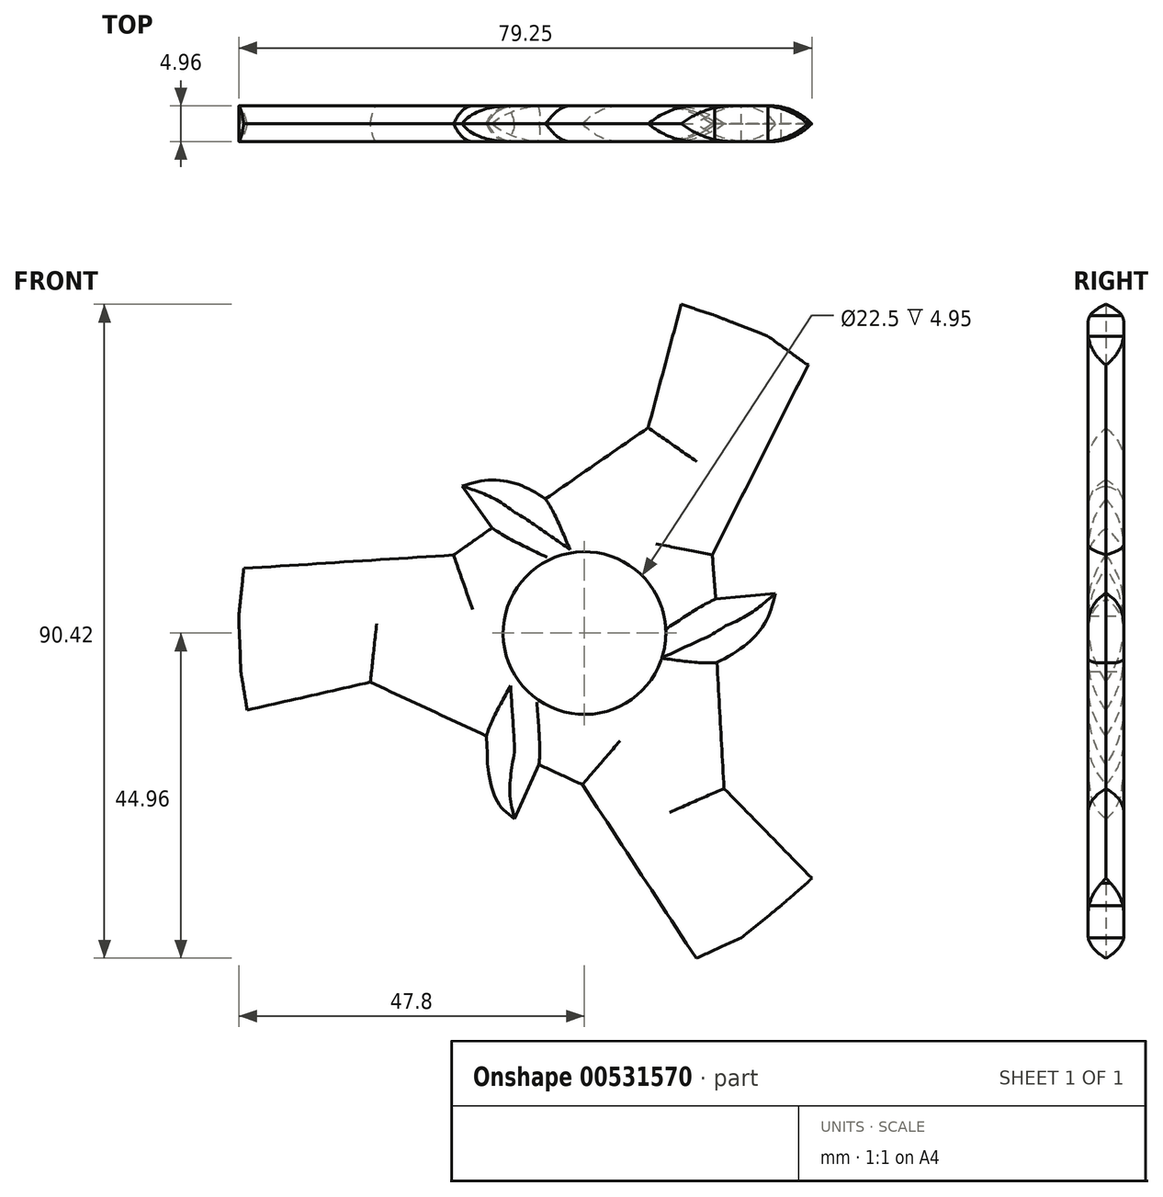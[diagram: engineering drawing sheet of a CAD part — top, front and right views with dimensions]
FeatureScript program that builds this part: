
annotation { "Feature Type Name" : "Feature", "Feature Type Description" : "" }
export const myFeature = defineFeature(function(context is Context, id is Id, definition is map)
    precondition{}
    {
        {
            var Q0;
            Q0=qCreatedBy(makeId("Front.planeOp"),FACE);
            var sketch = newSketch(context, id + "F0", { "sketchPlane" : qUnion([Q0])});
            skLineSegment(sketch, "E0", {"start": v(-60.3, 10.65) * mm, "end": v(-21.94, 13.1) * mm});
            skLineSegment(sketch, "E1", {"start": v(-60.3, 10.65) * mm, "end": v(-61.14, 2.7) * mm});
            skLineSegment(sketch, "E2", {"start": v(-61.14, 2.7) * mm, "end": v(-60.8, -6.3) * mm});
            skLineSegment(sketch, "E3", {"start": v(32.42, 52.48) * mm, "end": v(38.9, 47.8) * mm});
            skLineSegment(sketch, "E4", {"start": v(20.48, -57.17) * mm, "end": v(27.79, -53.9) * mm});
            skLineSegment(sketch, "E5", {"start": v(27.79, -53.9) * mm, "end": v(34.8, -48.28) * mm});
            skLineSegment(sketch, "E6", {"start": v(20.48, -57.17) * mm, "end": v(-0.35, -25.4) * mm});
            skLineSegment(sketch, "E7", {"start": v(-0.35, -25.4) * mm, "end": v(-7.62, -22.05) * mm});
            skLineSegment(sketch, "E8", {"start": v(-35.88, -8.21) * mm, "end": v(-59.64, -13.61) * mm});
            skLineSegment(sketch, "E9", {"start": v(23.4, -26.03) * mm, "end": v(40.2, -43.2) * mm});
            skLineSegment(sketch, "E10", {"start": v(-21.94, 13.1) * mm, "end": v(-15.4, 17.7) * mm});
            skLineSegment(sketch, "E11", {"start": v(10.69, 34.45) * mm, "end": v(17.05, 58.2) * mm});
            skLineSegment(sketch, "E12", {"start": v(17.05, 58.2) * mm, "end": v(32.42, 52.48) * mm});
            skLineSegment(sketch, "E13", {"start": v(40.2, -43.2) * mm, "end": v(34.8, -48.28) * mm});
            skLineSegment(sketch, "E14", {"start": v(-60.8, -6.3) * mm, "end": v(-59.64, -13.61) * mm});
            skPoint(sketch, "E15", {"position": v(-15.4, 17.7) * mm});
            skPoint(sketch, "E16", {"position": v(-7.62, -22.05) * mm});
            skPoint(sketch, "E17", {"position": v(-16.7, -17.87) * mm});
            skLineSegment(sketch, "E18", {"start": v(-57.1, 10.85) * mm, "end": v(-57.94, 2.9) * mm});
            skLineSegment(sketch, "E19", {"start": v(-57.94, 2.9) * mm, "end": v(-57.6, -6.44) * mm});
            skLineSegment(sketch, "E20", {"start": v(-57.6, -6.44) * mm, "end": v(-56.52, -12.9) * mm});
            skLineSegment(sketch, "E21", {"start": v(18.73, -54.5) * mm, "end": v(26.3, -51.08) * mm});
            skLineSegment(sketch, "E22", {"start": v(26.3, -51.08) * mm, "end": v(32.97, -45.66) * mm});
            skLineSegment(sketch, "E23", {"start": v(32.97, -45.66) * mm, "end": v(37.26, -41.92) * mm});
            skLineSegment(sketch, "E24", {"start": v(37.2, 45.1) * mm, "end": v(30.73, 49.77) * mm});
            skLineSegment(sketch, "E25", {"start": v(30.73, 49.77) * mm, "end": v(21.84, 53.25) * mm});
            skLineSegment(sketch, "E26", {"start": v(21.84, 53.25) * mm, "end": v(16.22, 55.1) * mm});
            skLineSegment(sketch, "E27.trimOffspring", {"start": v(21.84, 53.25) * mm, "end": v(22.04, 53.58) * mm});
            skLineSegment(sketch, "E28.trimOffspring", {"start": v(21.43, 13.1) * mm, "end": v(38.9, 47.8) * mm});
            skPoint(sketch, "E29", {"position": v(5.47, -9.54) * mm});
            skPoint(sketch, "E30.end.orphan", {"position": v(23.99, 55.62) * mm});
            skPoint(sketch, "E31", {"position": v(5.53, 9.51) * mm});
            skPoint(sketch, "E32", {"position": v(-11, 0.03) * mm});
            skLineSegment(sketch, "E33", {"start": v(-7.62, -22.05) * mm, "end": v(-11.72, -31.18) * mm});
            skPoint(sketch, "E34", {"position": v(-14, -29.12) * mm});
            skPoint(sketch, "E35", {"position": v(-15.5, -26.06) * mm});
            skPoint(sketch, "E36", {"position": v(-16.25, -22.11) * mm});
            skFitSpline(sketch, "E37", {"points": [v(-11.72, -31.18) * mm, v(-14, -29.12) * mm, v(-15.5, -26.06) * mm, v(-16.25, -22.11) * mm, v(-16.43, -17.26) * mm], "startDerivative": vector(-11.16, 10.33) * mm, "endDerivative": vector(-2.85, 43.72) * mm});
            skLineSegment(sketch, "E38", {"start": v(-16.43, -17.26) * mm, "end": v(-35.88, -8.21) * mm});
            skLineSegment(sketch, "E39", {"start": v(21.99, 5.7) * mm, "end": v(31.95, 6.64) * mm});
            skPoint(sketch, "E40", {"position": v(30.89, 3) * mm});
            skPoint(sketch, "E41", {"position": v(29.02, -0.03) * mm});
            skPoint(sketch, "E42", {"position": v(26.37, -2.45) * mm});
            skFitSpline(sketch, "E43", {"points": [v(31.95, 6.64) * mm, v(30.89, 3) * mm, v(29.02, -0.03) * mm, v(26.37, -2.45) * mm, v(22.2, -4.93) * mm], "startDerivative": vector(-3.5, -14.8) * mm, "endDerivative": vector(-14.01, -6.46) * mm});
            skLineSegment(sketch, "E44", {"start": v(23.4, -26.03) * mm, "end": v(22.2, -4.93) * mm});
            skLineSegment(sketch, "E45", {"start": v(-14.66, 16.51) * mm, "end": v(-20.5, 24.64) * mm});
            skPoint(sketch, "E46", {"position": v(-16.82, 25.56) * mm});
            skPoint(sketch, "E47", {"position": v(-13.27, 25.48) * mm});
            skPoint(sketch, "E48", {"position": v(-9.84, 24.42) * mm});
            skFitSpline(sketch, "E49", {"points": [v(-20.5, 24.64) * mm, v(-16.82, 25.56) * mm, v(-13.27, 25.48) * mm, v(-9.84, 24.42) * mm, v(-6.56, 22.47) * mm], "startDerivative": vector(14.54, 4.47) * mm, "endDerivative": vector(12.66, -8.83) * mm});
            skLineSegment(sketch, "E50", {"start": v(10.69, 34.45) * mm, "end": v(-6.56, 22.47) * mm});
            skLineSegment(sketch, "E51", {"start": v(23.99, 55.62) * mm, "end": v(17.05, 58.2) * mm});
            skLineSegment(sketch, "E52", {"start": v(37.2, 45.1) * mm, "end": v(37.5, 45) * mm});
            skLineSegment(sketch, "E53", {"start": v(37.26, -41.92) * mm, "end": v(38.12, -41.08) * mm});
            skLineSegment(sketch, "E54", {"start": v(21.43, 13.1) * mm, "end": v(21.99, 5.7) * mm});
            skLineSegment(sketch, "E55", {"start": v(-57.94, 2.9) * mm, "end": v(-61.14, 2.7) * mm});
            skSolve(sketch);
        }
        {
            var Q0;
            {var subQ6=sQuery(id+"F0.wireOp",EDGE,"E7");Q0=makeQuery(id+"F0.imprint","IMPRINT",FACE,{"disambiguationData":[TD([[makeQuery(id+"F0.imprint","IMPRINT",EDGE,{"derivedFrom":subQ6}),-1.0]])]});}
            extrude(context, id + "F1", {"entities" : qUnion([Q0]), "depth" : 3 * mm, "offsetDistance" : 25 * mm});
        }
        {
            var Q0;
            Q0=makeQuery(id+"F1.opExtrude","CAP_FACE",FACE,{"disambiguationData":[OSD([sQuery(id+"F0.wireOp",EDGE,"E0"),sQuery(id+"F0.wireOp",EDGE,"E6"),sQuery(id+"F0.wireOp",EDGE,"E7"),sQuery(id+"F0.wireOp",EDGE,"E8"),sQuery(id+"F0.wireOp",EDGE,"7ChtSRiK-8qqs-AgvX-7XEc-J2jZBFgeAv2A"),sQuery(id+"F0.wireOp",EDGE,"E9"),sQuery(id+"F0.wireOp",EDGE,"E10"),sQuery(id+"F0.wireOp",EDGE,"E11"),sQuery(id+"F0.wireOp",EDGE,"ZQRVfp4O-9mxL-yRTk-LCVP-vJVHwubdKNsi"),sQuery(id+"F0.wireOp",EDGE,"0jEqfjd1-e5fq-yYwF-8Nno-jkrp0ULIgv4y"),sQuery(id+"F0.wireOp",EDGE,"JVot5bSo-Colf-nkQM-OlhC-5Es9wFrioCPp"),sQuery(id+"F0.wireOp",EDGE,"UVis2Jix-gy3t-cIvo-fX3M-bqyRfmCnqcsT"),sQuery(id+"F0.wireOp",EDGE,"75dDdgBk-M5Ql-q7eO-8fkK-rJfClx9eH0YD"),sQuery(id+"F0.wireOp",EDGE,"HJNizCUg-wDDe-gmiW-IziM-RZFIlMrWVAXs"),sQuery(id+"F0.wireOp",EDGE,"NF2K1iKp-8O8z-xlyG-eYtL-JkH1SoewVlyn"),sQuery(id+"F0.wireOp",EDGE,"E18"),sQuery(id+"F0.wireOp",EDGE,"E19"),sQuery(id+"F0.wireOp",EDGE,"E20"),sQuery(id+"F0.wireOp",EDGE,"E21"),sQuery(id+"F0.wireOp",EDGE,"E22"),sQuery(id+"F0.wireOp",EDGE,"E23"),sQuery(id+"F0.wireOp",EDGE,"E24"),sQuery(id+"F0.wireOp",EDGE,"E25"),sQuery(id+"F0.wireOp",EDGE,"E26"),sQuery(id+"F0.wireOp",EDGE,"E28.trimOffspring"),sQuery(id+"F0.wireOp",EDGE,"f8071829-f0c0-4542-9b0a-bcae6590e0a6.trimOffspring"),sQuery(id+"F0.wireOp",EDGE,"0ea21267-62f8-427a-be6e-8f7893526f82.trimOffspring"),sQuery(id+"F0.wireOp",EDGE,"b5eeae89-63d8-48f1-8cd6-2f1344065213.trimOffspring")])],"isStart":false});
            var sketch = newSketch(context, id + "F2", { "sketchPlane" : qUnion([Q0])});
            skLineSegment(sketch, "E56", {"start": v(-16.43, -17.26) * mm, "end": v(-7.62, -22.05) * mm});
            skLineSegment(sketch, "E57", {"start": v(-15.47, 17.64) * mm, "end": v(-6.56, 22.47) * mm});
            skLineSegment(sketch, "E58", {"start": v(21.99, 5.7) * mm, "end": v(22.2, -4.93) * mm});
            skLineSegment(sketch, "E59", {"start": v(-12.02, -19.66) * mm, "end": v(-5.77, -8.17) * mm});
            skLineSegment(sketch, "E60", {"start": v(22.1, 0.39) * mm, "end": v(10, 0.14) * mm});
            skLineSegment(sketch, "E61", {"start": v(-11.02, 20.06) * mm, "end": v(-4.87, 8.73) * mm});
            skLineSegment(sketch, "E62", {"start": v(-20.5, 24.64) * mm, "end": v(-11.02, 20.06) * mm});
            skLineSegment(sketch, "E63", {"start": v(22.1, 0.39) * mm, "end": v(31.95, 6.64) * mm});
            skLineSegment(sketch, "E64", {"start": v(-12.02, -19.66) * mm, "end": v(-11.72, -31.18) * mm});
            skLineSegment(sketch, "E65", {"start": v(30.73, 49.77) * mm, "end": v(7.44, 6.68) * mm});
            skLineSegment(sketch, "E66", {"start": v(-57.94, 2.9) * mm, "end": v(-9.57, 2.9) * mm});
            skLineSegment(sketch, "E67", {"start": v(26.3, -51.08) * mm, "end": v(2.03, -9.8) * mm});
            skSolve(sketch);
        }
        {
            var Q0;
            Q0=makeQuery(id+"F1.opExtrude","CAP_EDGE",EDGE,{"disambiguationData":[OSD([sQuery(id+"F0.wireOp",EDGE,"E8")])],"isStart":false});
            var Q1;
            Q1=makeQuery(id+"F1.opExtrude","CAP_EDGE",EDGE,{"disambiguationData":[OSD([sQuery(id+"F0.wireOp",EDGE,"E38")])],"isStart":false});
            var Q2;
            Q2=makeQuery(id+"F1.opExtrude","CAP_EDGE",EDGE,{"disambiguationData":[OSD([sQuery(id+"F0.wireOp",EDGE,"E0")])],"isStart":false});
            var Q3;
            Q3=makeQuery(id+"F1.opExtrude","CAP_EDGE",EDGE,{"disambiguationData":[OSD([sQuery(id+"F0.wireOp",EDGE,"E10")])],"isStart":false});
            var Q4;
            Q4=makeQuery(id+"F1.opExtrude","CAP_EDGE",EDGE,{"disambiguationData":[OSD([sQuery(id+"F0.wireOp",EDGE,"E50")])],"isStart":false});
            var Q5;
            Q5=makeQuery(id+"F1.opExtrude","CAP_EDGE",EDGE,{"disambiguationData":[OSD([sQuery(id+"F0.wireOp",EDGE,"E11")])],"isStart":false});
            var Q6;
            Q6=makeQuery(id+"F1.opExtrude","CAP_EDGE",EDGE,{"disambiguationData":[OSD([sQuery(id+"F0.wireOp",EDGE,"E28.trimOffspring")])],"isStart":false});
            var Q7;
            Q7=makeQuery(id+"F1.opExtrude","CAP_EDGE",EDGE,{"disambiguationData":[OSD([sQuery(id+"F0.wireOp",EDGE,"E54")])],"isStart":false});
            var Q8;
            Q8=makeQuery(id+"F1.opExtrude","CAP_EDGE",EDGE,{"disambiguationData":[OSD([sQuery(id+"F0.wireOp",EDGE,"E44")])],"isStart":false});
            var Q9;
            Q9=makeQuery(id+"F1.opExtrude","CAP_EDGE",EDGE,{"disambiguationData":[OSD([sQuery(id+"F0.wireOp",EDGE,"E9")])],"isStart":false});
            var Q10;
            Q10=makeQuery(id+"F1.opExtrude","CAP_EDGE",EDGE,{"disambiguationData":[OSD([sQuery(id+"F0.wireOp",EDGE,"E6")])],"isStart":false});
            var Q11;
            Q11=makeQuery(id+"F1.opExtrude","CAP_EDGE",EDGE,{"disambiguationData":[OSD([sQuery(id+"F0.wireOp",EDGE,"E7")])],"isStart":false});
            fillet(context, id + "F3", {"entities" : qUnion([Q0, Q1, Q2, Q3, Q4, Q5, Q6, Q7, Q8, Q9, Q10, Q11]), "radius" : 16 * mm, "tangentPropagation" : true, "rho" : 0.5, "crossSection" : FilletCrossSection.CONIC, "allowEdgeOverflow" : false});
        }
        {
            var Q0;
            Q0=makeQuery(id+"F1.opExtrude","CAP_EDGE",EDGE,{"disambiguationData":[OSD([sQuery(id+"F0.wireOp",EDGE,"E43")])],"isStart":false});
            var Q1;
            Q1=makeQuery(id+"F1.opExtrude","CAP_EDGE",EDGE,{"disambiguationData":[OSD([sQuery(id+"F0.wireOp",EDGE,"E49")])],"isStart":false});
            var Q2;
            Q2=makeQuery(id+"F1.opExtrude","CAP_EDGE",EDGE,{"disambiguationData":[OSD([sQuery(id+"F0.wireOp",EDGE,"E37")])],"isStart":false});
            var Q3;
            Q3=makeQuery(id+"F1.opExtrude","CAP_EDGE",EDGE,{"disambiguationData":[OSD([sQuery(id+"F0.wireOp",EDGE,"E45")])],"isStart":false});
            var Q4;
            Q4=makeQuery(id+"F1.opExtrude","CAP_EDGE",EDGE,{"disambiguationData":[OSD([sQuery(id+"F0.wireOp",EDGE,"E33")])],"isStart":false});
            var Q5;
            Q5=makeQuery(id+"F1.opExtrude","CAP_EDGE",EDGE,{"disambiguationData":[OSD([sQuery(id+"F0.wireOp",EDGE,"E39")])],"isStart":false});
            fillet(context, id + "F4", {"entities" : qUnion([Q0, Q1, Q2, Q3, Q4, Q5]), "radius" : 5 * mm, "tangentPropagation" : true, "allowEdgeOverflow" : false});
        }
        {
            var Q0;
            Q0=makeQuery(id+"F1.opExtrude","SWEPT_BODY",BODY,{"disambiguationData":[OSD([sQuery(id+"F0.wireOp",EDGE,"E0"),sQuery(id+"F0.wireOp",EDGE,"E6"),sQuery(id+"F0.wireOp",EDGE,"E7"),sQuery(id+"F0.wireOp",EDGE,"E8"),sQuery(id+"F0.wireOp",EDGE,"E9"),sQuery(id+"F0.wireOp",EDGE,"E10"),sQuery(id+"F0.wireOp",EDGE,"E11"),sQuery(id+"F0.wireOp",EDGE,"NF2K1iKp-8O8z-xlyG-eYtL-JkH1SoewVlyn"),sQuery(id+"F0.wireOp",EDGE,"E18"),sQuery(id+"F0.wireOp",EDGE,"E19"),sQuery(id+"F0.wireOp",EDGE,"E20"),sQuery(id+"F0.wireOp",EDGE,"E21"),sQuery(id+"F0.wireOp",EDGE,"E22"),sQuery(id+"F0.wireOp",EDGE,"E23"),sQuery(id+"F0.wireOp",EDGE,"E24"),sQuery(id+"F0.wireOp",EDGE,"E25"),sQuery(id+"F0.wireOp",EDGE,"E26"),sQuery(id+"F0.wireOp",EDGE,"E28.trimOffspring"),sQuery(id+"F0.wireOp",EDGE,"E33"),sQuery(id+"F0.wireOp",EDGE,"E37"),sQuery(id+"F0.wireOp",EDGE,"E38"),sQuery(id+"F0.wireOp",EDGE,"E39"),sQuery(id+"F0.wireOp",EDGE,"E43"),sQuery(id+"F0.wireOp",EDGE,"E44"),sQuery(id+"F0.wireOp",EDGE,"E45"),sQuery(id+"F0.wireOp",EDGE,"E49"),sQuery(id+"F0.wireOp",EDGE,"E50"),sQuery(id+"F0.wireOp",EDGE,"E52"),sQuery(id+"F0.wireOp",EDGE,"E53"),sQuery(id+"F0.wireOp",EDGE,"E54")])]});
            var Q1;
            Q1=qCreatedBy(makeId("Front.planeOp"),FACE);
            mirror(context, id + "F5", {"operationType" : NewBodyOperationType.ADD, "entities" : qUnion([Q0]), "mirrorPlane" : qUnion([Q1])});
        }
        {
            var Q0;
            Q0=makeQuery(id+"F1.opExtrude","SWEPT_BODY",BODY,{"disambiguationData":[OSD([sQuery(id+"F0.wireOp",EDGE,"E0"),sQuery(id+"F0.wireOp",EDGE,"E6"),sQuery(id+"F0.wireOp",EDGE,"E7"),sQuery(id+"F0.wireOp",EDGE,"E8"),sQuery(id+"F0.wireOp",EDGE,"E9"),sQuery(id+"F0.wireOp",EDGE,"E10"),sQuery(id+"F0.wireOp",EDGE,"E11"),sQuery(id+"F0.wireOp",EDGE,"NF2K1iKp-8O8z-xlyG-eYtL-JkH1SoewVlyn"),sQuery(id+"F0.wireOp",EDGE,"E18"),sQuery(id+"F0.wireOp",EDGE,"E19"),sQuery(id+"F0.wireOp",EDGE,"E20"),sQuery(id+"F0.wireOp",EDGE,"E21"),sQuery(id+"F0.wireOp",EDGE,"E22"),sQuery(id+"F0.wireOp",EDGE,"E23"),sQuery(id+"F0.wireOp",EDGE,"E24"),sQuery(id+"F0.wireOp",EDGE,"E25"),sQuery(id+"F0.wireOp",EDGE,"E26"),sQuery(id+"F0.wireOp",EDGE,"E28.trimOffspring"),sQuery(id+"F0.wireOp",EDGE,"E33"),sQuery(id+"F0.wireOp",EDGE,"E37"),sQuery(id+"F0.wireOp",EDGE,"E38"),sQuery(id+"F0.wireOp",EDGE,"E39"),sQuery(id+"F0.wireOp",EDGE,"E43"),sQuery(id+"F0.wireOp",EDGE,"E44"),sQuery(id+"F0.wireOp",EDGE,"E45"),sQuery(id+"F0.wireOp",EDGE,"E49"),sQuery(id+"F0.wireOp",EDGE,"E50"),sQuery(id+"F0.wireOp",EDGE,"E52"),sQuery(id+"F0.wireOp",EDGE,"E53"),sQuery(id+"F0.wireOp",EDGE,"E54")])]});
            var Q1;
            Q1=qCreatedBy(makeId("Origin.pointOp"),VERTEX);
            transform(context, id + "F6", {"entities" : qUnion([Q0]), "transformType" : TransformType.SCALE_UNIFORMLY, "scale" : 0.82, "scalePoint" : qUnion([Q1]), "makeCopy" : false});
        }
        {
            var Q0;
            Q0=makeQuery(id+"F2.imprint","IMPRINT",FACE,{"disambiguationData":[TD([[makeQuery(id+"F2.imprint","IMPRINT",EDGE,{"derivedFrom":makeQuery(id+"F1.opExtrude","CAP_EDGE",EDGE,{"disambiguationData":[OSD([sQuery(id+"F0.wireOp",EDGE,"E0")])],"isStart":false})}),-1.0]])]});
            var sketch = newSketch(context, id + "F7", { "sketchPlane" : qUnion([Q0])});
            skCircle(sketch, "E68", {"center": v(0, 0) * mm, "radius": 11.25 * mm});
            skSolve(sketch);
        }
        {
            var Q0;
            Q0 = qSketchRegion(id + "F7", true);
            extrude(context, id + "F8", {"entities" : qUnion([Q0]), "operationType" : NewBodyOperationType.REMOVE, "oppositeDirection" : true, "depth" : 25 * mm, "offsetDistance" : 25 * mm});
        }
    });
